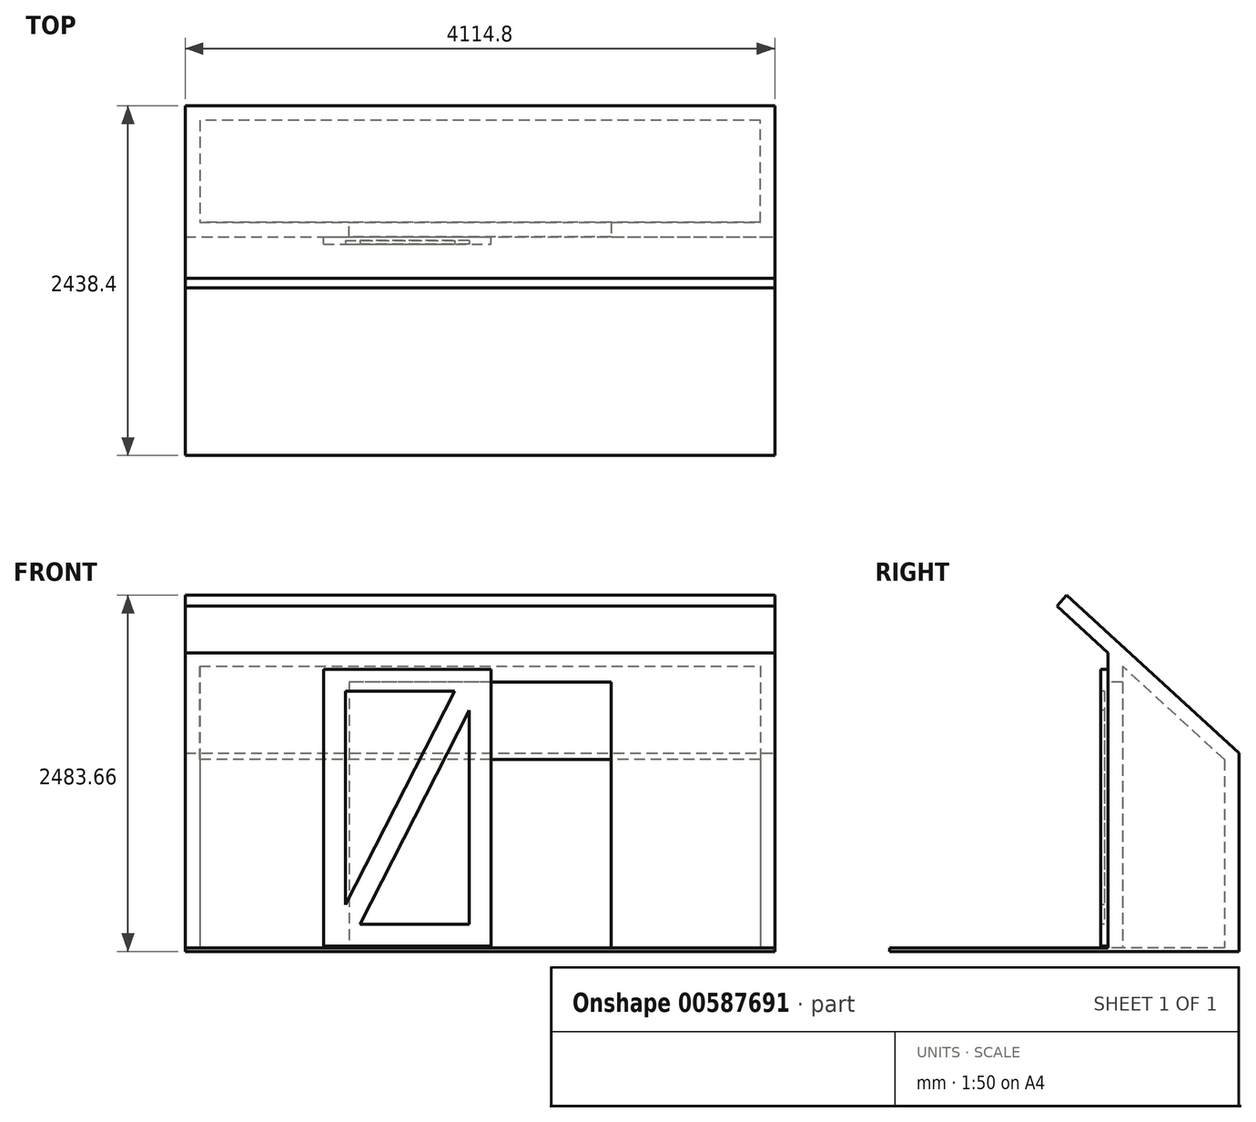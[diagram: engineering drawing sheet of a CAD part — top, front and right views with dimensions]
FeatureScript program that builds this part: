
annotation { "Feature Type Name" : "Feature", "Feature Type Description" : "" }
export const myFeature = defineFeature(function(context is Context, id is Id, definition is map)
    precondition{}
    {
        {
            var Q0;
            Q0=qCreatedBy(makeId("Top.planeOp"),FACE);
            var sketch = newSketch(context, id + "F0", { "sketchPlane" : qUnion([Q0])});
            skLineSegment(sketch, "E0.bottom", {"start": v(0, 0) * mm, "end": v(4114.8, 0) * mm});
            skLineSegment(sketch, "E0.top", {"start": v(0, -2438.4) * mm, "end": v(4114.8, -2438.4) * mm});
            skLineSegment(sketch, "E0.left", {"start": v(0, 0) * mm, "end": v(0, -2438.4) * mm});
            skLineSegment(sketch, "E0.right", {"start": v(4114.8, 0) * mm, "end": v(4114.8, -2438.4) * mm});
            skSolve(sketch);
        }
        {
            var Q0;
            Q0=makeQuery(id+"F0.imprint","IMPRINT",FACE,{"disambiguationData":[TD([[makeQuery(id+"F0.imprint","IMPRINT",EDGE,{"derivedFrom":sQuery(id+"F0.wireOp",EDGE,"E0.bottom")}),-1.0]])]});
            extrude(context, id + "F1", {"entities" : qUnion([Q0]), "oppositeDirection" : true, "depth" : 25.4 * mm, "offsetDistance" : 25.4 * mm});
        }
        {
            var Q0;
            Q0=makeQuery(id+"F1.opExtrude","CAP_FACE",FACE,{"disambiguationData":[OSD([sQuery(id+"F0.wireOp",EDGE,"E0.bottom"),sQuery(id+"F0.wireOp",EDGE,"E0.top"),sQuery(id+"F0.wireOp",EDGE,"E0.left"),sQuery(id+"F0.wireOp",EDGE,"E0.right")])],"isStart":true});
            var sketch = newSketch(context, id + "F2", { "sketchPlane" : qUnion([Q0])});
            skLineSegment(sketch, "E1.bottom", {"start": v(4114.8, 0) * mm, "end": v(0, 0) * mm});
            skLineSegment(sketch, "E1.left", {"start": v(4114.8, 0) * mm, "end": v(4114.8, -914.4) * mm});
            skLineSegment(sketch, "E1.right", {"start": v(0, 0) * mm, "end": v(0, -914.4) * mm});
            skLineSegment(sketch, "E2", {"start": v(0, -914.4) * mm, "end": v(1143, -914.4) * mm});
            skLineSegment(sketch, "E3", {"start": v(1143, -914.4) * mm, "end": v(1143, -812.8) * mm});
            skLineSegment(sketch, "E4", {"start": v(1143, -812.8) * mm, "end": v(101.6, -812.8) * mm});
            skLineSegment(sketch, "E5", {"start": v(101.6, -812.8) * mm, "end": v(101.6, -101.6) * mm});
            skLineSegment(sketch, "E6", {"start": v(101.6, -101.6) * mm, "end": v(4013.2, -101.6) * mm});
            skLineSegment(sketch, "E7", {"start": v(4013.2, -101.6) * mm, "end": v(4013.2, -812.8) * mm});
            skLineSegment(sketch, "E8", {"start": v(4013.2, -812.8) * mm, "end": v(2971.8, -812.8) * mm});
            skLineSegment(sketch, "E9", {"start": v(2971.8, -812.8) * mm, "end": v(2971.8, -914.4) * mm});
            skLineSegment(sketch, "E10", {"start": v(2971.8, -914.4) * mm, "end": v(4114.8, -914.4) * mm});
            skSolve(sketch);
        }
        {
            var Q0;
            Q0=makeQuery(id+"F2.imprint","IMPRINT",FACE,{"disambiguationData":[TD([[makeQuery(id+"F2.imprint","IMPRINT",EDGE,{"derivedFrom":sQuery(id+"F2.wireOp",EDGE,"E1.bottom")}),-1.0]])]});
            extrude(context, id + "F3", {"entities" : qUnion([Q0]), "operationType" : NewBodyOperationType.ADD, "flatOperationType" : FlatOperationType.REMOVE, "depth" : 2057.4 * mm, "offsetDistance" : 25.4 * mm, "domain" : OperationDomain.MODEL});
        }
        {
            var Q0;
            Q0=makeQuery(id+"F3.boolean.opBoolean","MERGE",FACE,{"derivedFrom":[makeQuery(id+"F1.opExtrude","SWEPT_FACE",FACE,{"disambiguationData":[OSD([sQuery(id+"F0.wireOp",EDGE,"E0.right")])]}),makeQuery(id+"F3.opExtrude","SWEPT_FACE",FACE,{"disambiguationData":[OSD([sQuery(id+"F2.wireOp",EDGE,"E1.left")])]})]});
            var sketch = newSketch(context, id + "F4", { "sketchPlane" : qUnion([Q0])});
            skLineSegment(sketch, "E11", {"start": v(-914.4, 2057.4) * mm, "end": v(0, 1219.2) * mm});
            skLineSegment(sketch, "E12", {"start": v(0, 1219.2) * mm, "end": v(0, 2057.4) * mm});
            skLineSegment(sketch, "E13", {"start": v(0, 2057.4) * mm, "end": v(-914.4, 2057.4) * mm});
            skSolve(sketch);
        }
        {
            var Q0;
            Q0=makeQuery(id+"F4.imprint","IMPRINT",FACE,{"disambiguationData":[TD([[makeQuery(id+"F4.imprint","IMPRINT",EDGE,{"derivedFrom":sQuery(id+"F4.wireOp",EDGE,"E11")}),1.0]])]});
            extrude(context, id + "F5", {"entities" : qUnion([Q0]), "operationType" : NewBodyOperationType.REMOVE, "endBound" : BoundingType.THROUGH_ALL, "oppositeDirection" : true, "depth" : 25.4 * mm, "offsetDistance" : 25.4 * mm});
        }
        {
            var Q0;
            Q0=makeQuery(id+"F3.boolean.opBoolean","MERGE",FACE,{"derivedFrom":[makeQuery(id+"F1.opExtrude","SWEPT_FACE",FACE,{"disambiguationData":[OSD([sQuery(id+"F0.wireOp",EDGE,"E0.right")])]}),makeQuery(id+"F3.opExtrude","SWEPT_FACE",FACE,{"disambiguationData":[OSD([sQuery(id+"F2.wireOp",EDGE,"E1.left")])]})]});
            var sketch = newSketch(context, id + "F6", { "sketchPlane" : qUnion([Q0])});
            skLineSegment(sketch, "E14", {"start": v(0, 1219.2) * mm, "end": v(-1270, 2383.37) * mm});
            skLineSegment(sketch, "E15", {"start": v(-1270, 2383.37) * mm, "end": v(-1201.35, 2458.26) * mm});
            skLineSegment(sketch, "E16", {"start": v(-1201.35, 2458.26) * mm, "end": v(0, 1357.03) * mm});
            skLineSegment(sketch, "E17", {"start": v(0, 1357.03) * mm, "end": v(0, 1219.2) * mm});
            skSolve(sketch);
        }
        {
            var Q0;
            {var subQ0=sQuery(id+"F6.wireOp",EDGE,"E15");Q0=makeQuery(id+"F6.imprint","IMPRINT",FACE,{"disambiguationData":[TD([[makeQuery(id+"F6.imprint","IMPRINT",EDGE,{"derivedFrom":subQ0}),-1.0]])]});}
            var Q1;
            Q1=makeQuery(id+"F3.boolean.opBoolean","MERGE",FACE,{"derivedFrom":[makeQuery(id+"F1.opExtrude","SWEPT_FACE",FACE,{"disambiguationData":[OSD([sQuery(id+"F0.wireOp",EDGE,"E0.left")])]}),makeQuery(id+"F3.opExtrude","SWEPT_FACE",FACE,{"disambiguationData":[OSD([sQuery(id+"F2.wireOp",EDGE,"E1.right")])]})]});
            extrude(context, id + "F7", {"entities" : qUnion([Q0]), "operationType" : NewBodyOperationType.ADD, "endBound" : BoundingType.UP_TO_SURFACE, "oppositeDirection" : true, "depth" : 25.4 * mm, "endBoundEntityFace" : qUnion([Q1]), "offsetDistance" : 25.4 * mm});
        }
        {
            var Q0;
            Q0=makeQuery(id+"F3.opExtrude","SWEPT_FACE",FACE,{"disambiguationData":[OSD([sQuery(id+"F2.wireOp",EDGE,"E2")])]});
            var sketch = newSketch(context, id + "F8", { "sketchPlane" : qUnion([Q0])});
            skLineSegment(sketch, "E18.0", {"start": v(2971.8, 2057.4) * mm, "end": v(2971.8, 0) * mm});
            skLineSegment(sketch, "E19.bottom", {"start": v(2971.8, 2057.4) * mm, "end": v(1143, 2057.4) * mm});
            skLineSegment(sketch, "E19.top", {"start": v(2971.8, 1854.2) * mm, "end": v(1143, 1854.2) * mm});
            skLineSegment(sketch, "E19.left", {"start": v(2971.8, 2057.4) * mm, "end": v(2971.8, 1854.2) * mm});
            skLineSegment(sketch, "E19.right", {"start": v(1143, 2057.4) * mm, "end": v(1143, 1854.2) * mm});
            skSolve(sketch);
        }
        {
            var Q0;
            Q0=makeQuery(id+"F8.imprint","IMPRINT",FACE,{"disambiguationData":[TD([[makeQuery(id+"F8.imprint","IMPRINT",EDGE,{"derivedFrom":sQuery(id+"F8.wireOp",EDGE,"E19.bottom")}),1.0]])]});
            extrude(context, id + "F9", {"entities" : qUnion([Q0]), "operationType" : NewBodyOperationType.ADD, "oppositeDirection" : true, "depth" : 101.6 * mm, "offsetDistance" : 25.4 * mm});
        }
        {
            var Q0;
            Q0=makeQuery(id+"F9.boolean.opBoolean","MERGE",FACE,{"derivedFrom":[makeQuery(id+"F3.opExtrude","SWEPT_FACE",FACE,{"disambiguationData":[OSD([sQuery(id+"F2.wireOp",EDGE,"E2")])]}),makeQuery(id+"F3.opExtrude","SWEPT_FACE",FACE,{"disambiguationData":[OSD([sQuery(id+"F2.wireOp",EDGE,"E10")])]}),makeQuery(id+"F9.opExtrude","CAP_FACE",FACE,{"disambiguationData":[OSD([sQuery(id+"F8.wireOp",EDGE,"E19.bottom"),sQuery(id+"F8.wireOp",EDGE,"E19.top"),sQuery(id+"F8.wireOp",EDGE,"E19.left"),sQuery(id+"F8.wireOp",EDGE,"E19.right")])],"isStart":true})]});
            var sketch = newSketch(context, id + "F10", { "sketchPlane" : qUnion([Q0])});
            skLineSegment(sketch, "E20.bottom", {"start": v(203.2, 1117.6) * mm, "end": v(812.8, 1117.6) * mm});
            skLineSegment(sketch, "E20.top", {"start": v(203.2, 203.2) * mm, "end": v(812.8, 203.2) * mm});
            skLineSegment(sketch, "E20.left", {"start": v(203.2, 1117.6) * mm, "end": v(203.2, 203.2) * mm});
            skLineSegment(sketch, "E20.right", {"start": v(812.8, 1117.6) * mm, "end": v(812.8, 203.2) * mm});
            skLineSegment(sketch, "E21.bottom", {"start": v(3302, 1117.6) * mm, "end": v(3911.6, 1117.6) * mm});
            skLineSegment(sketch, "E21.top", {"start": v(3302, 203.2) * mm, "end": v(3911.6, 203.2) * mm});
            skLineSegment(sketch, "E21.left", {"start": v(3302, 1117.6) * mm, "end": v(3302, 203.2) * mm});
            skLineSegment(sketch, "E21.right", {"start": v(3911.6, 1117.6) * mm, "end": v(3911.6, 203.2) * mm});
            skSolve(sketch);
        }
        {
            var Q0;
            Q0=makeQuery(id+"F9.boolean.opBoolean","MERGE",FACE,{"derivedFrom":[makeQuery(id+"F3.opExtrude","SWEPT_FACE",FACE,{"disambiguationData":[OSD([sQuery(id+"F2.wireOp",EDGE,"E2")])]}),makeQuery(id+"F3.opExtrude","SWEPT_FACE",FACE,{"disambiguationData":[OSD([sQuery(id+"F2.wireOp",EDGE,"E10")])]}),makeQuery(id+"F9.opExtrude","CAP_FACE",FACE,{"disambiguationData":[OSD([sQuery(id+"F8.wireOp",EDGE,"E19.bottom"),sQuery(id+"F8.wireOp",EDGE,"E19.top"),sQuery(id+"F8.wireOp",EDGE,"E19.left"),sQuery(id+"F8.wireOp",EDGE,"E19.right")])],"isStart":true})]});
            var sketch = newSketch(context, id + "F11", { "sketchPlane" : qUnion([Q0])});
            skLineSegment(sketch, "E22.bottom", {"start": v(965.2, 1943.1) * mm, "end": v(2133.6, 1943.1) * mm});
            skLineSegment(sketch, "E22.top", {"start": v(965.2, 12.7) * mm, "end": v(2133.6, 12.7) * mm});
            skLineSegment(sketch, "E22.left", {"start": v(965.2, 1943.1) * mm, "end": v(965.2, 12.7) * mm});
            skLineSegment(sketch, "E22.right", {"start": v(2133.6, 1943.1) * mm, "end": v(2133.6, 12.7) * mm});
            skSolve(sketch);
        }
        {
            var Q0;
            {var subQ1=sQuery(id+"F11.wireOp",EDGE,"E22.bottom");Q0=makeQuery(id+"F11.imprint","IMPRINT",FACE,{"disambiguationData":[TD([[makeQuery(id+"F11.imprint","IMPRINT",EDGE,{"derivedFrom":subQ1}),-1.0]])]});}
            var Q1;
            {var subQ0=sQuery(id+"F11.wireOp",EDGE,"E22.right");var subQ1=sQuery(id+"F11.wireOp",EDGE,"E22.top");var subQ2=makeQuery(id+"F11.imprint","INTERSECT",VERTEX,{"derivedFrom":[subQ1,subQ0]});Q1=makeQuery(id+"F11.imprint","IMPRINT",FACE,{"disambiguationData":[TD([[makeQuery(id+"F11.imprint","IMPRINT",EDGE,{"disambiguationData":[TD([[subQ2,1.0]])],"derivedFrom":subQ0}),-1.0]])]});}
            extrude(context, id + "F12", {"entities" : qUnion([Q0, Q1]), "depth" : 50.8 * mm, "offsetDistance" : 25.4 * mm});
        }
        {
            var Q0;
            Q0=makeQuery(id+"F12.opExtrude","CAP_FACE",FACE,{"disambiguationData":[OSD([sQuery(id+"F11.wireOp",EDGE,"E22.bottom"),sQuery(id+"F11.wireOp",EDGE,"E22.top"),sQuery(id+"F11.wireOp",EDGE,"E22.left"),sQuery(id+"F11.wireOp",EDGE,"E22.right")])],"isStart":false});
            var sketch = newSketch(context, id + "F13", { "sketchPlane" : qUnion([Q0])});
            skLineSegment(sketch, "E23.bottom", {"start": v(1117.6, 1790.7) * mm, "end": v(1981.2, 1790.7) * mm});
            skLineSegment(sketch, "E23.top", {"start": v(1117.6, 165.1) * mm, "end": v(1981.2, 165.1) * mm});
            skLineSegment(sketch, "E23.left", {"start": v(1117.6, 1790.7) * mm, "end": v(1117.6, 165.1) * mm});
            skLineSegment(sketch, "E23.right", {"start": v(1981.2, 1790.7) * mm, "end": v(1981.2, 165.1) * mm});
            skLineSegment(sketch, "E24", {"start": v(1879.6, 1790.7) * mm, "end": v(1117.6, 301.12) * mm});
            skLineSegment(sketch, "E25", {"start": v(1981.2, 1654.68) * mm, "end": v(1219.2, 165.1) * mm});
            skSolve(sketch);
        }
        {
            var Q0;
            {var subQ3=sQuery(id+"F13.wireOp",EDGE,"E24");Q0=makeQuery(id+"F13.imprint","IMPRINT",FACE,{"disambiguationData":[TD([[makeQuery(id+"F13.imprint","IMPRINT",EDGE,{"derivedFrom":subQ3}),-1.0]])]});}
            var Q1;
            {var subQ3=sQuery(id+"F13.wireOp",EDGE,"E25");Q1=makeQuery(id+"F13.imprint","IMPRINT",FACE,{"disambiguationData":[TD([[makeQuery(id+"F13.imprint","IMPRINT",EDGE,{"derivedFrom":subQ3}),1.0]])]});}
            extrude(context, id + "F14", {"entities" : qUnion([Q0, Q1]), "operationType" : NewBodyOperationType.REMOVE, "oppositeDirection" : true, "depth" : 25.4 * mm, "offsetDistance" : 25.4 * mm});
        }
    });
